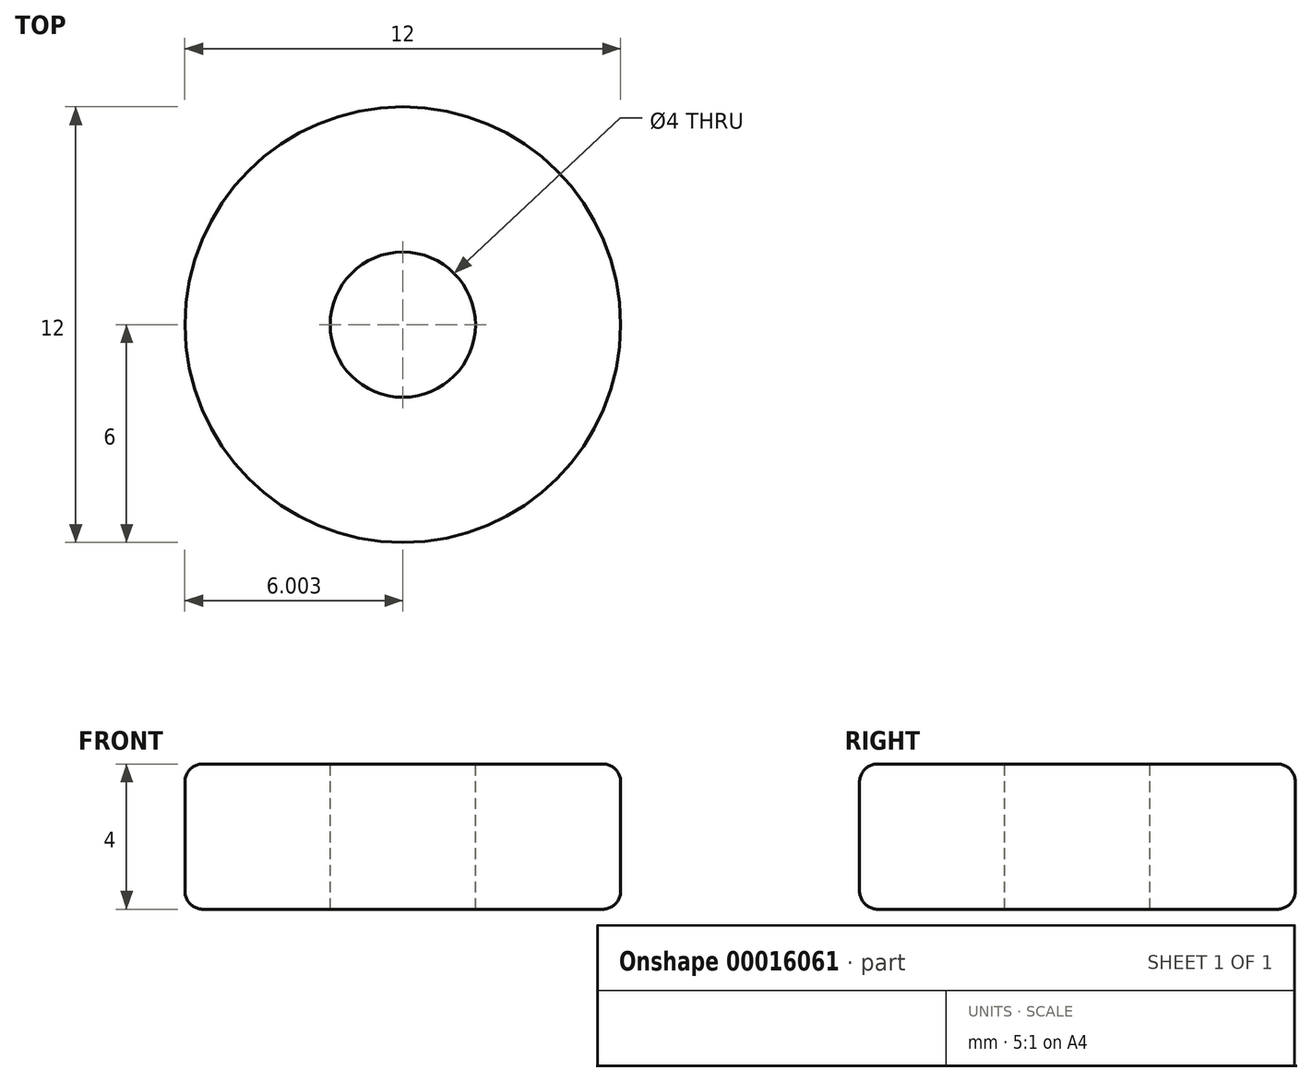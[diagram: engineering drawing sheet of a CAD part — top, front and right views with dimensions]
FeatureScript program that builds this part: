
annotation { "Feature Type Name" : "Feature", "Feature Type Description" : "" }
export const myFeature = defineFeature(function(context is Context, id is Id, definition is map)
    precondition{}
    {
        {
            var Q0;
            Q0=qCreatedBy(makeId("Top.planeOp"),FACE);
            var sketch = newSketch(context, id + "F0", { "sketchPlane" : qUnion([Q0])});
            skCircle(sketch, "E0", {"center": v(-26.95, 0) * mm, "radius": 6 * mm});
            skSolve(sketch);
        }
        {
            var Q0;
            Q0 = qSketchRegion(id + "F0", true);
            extrude(context, id + "F1", {"entities" : qUnion([Q0]), "depth" : 4 * mm});
        }
        {
            var Q0;
            Q0=makeQuery(id+"F1.opExtrude","CAP_FACE",FACE,{"disambiguationData":[OSD([sQuery(id+"F0.wireOp",EDGE,"E0")])],"isStart":false});
            var sketch = newSketch(context, id + "F2", { "sketchPlane" : qUnion([Q0])});
            skCircle(sketch, "E1", {"center": v(-26.95, 0) * mm, "radius": 2 * mm});
            skSolve(sketch);
        }
        {
            var Q0;
            Q0 = qSketchRegion(id + "F2", true);
            extrude(context, id + "F3", {"entities" : qUnion([Q0]), "operationType" : NewBodyOperationType.REMOVE, "endBound" : BoundingType.THROUGH_ALL, "oppositeDirection" : true, "depth" : 25 * mm});
        }
        {
            var Q0;
            Q0=makeQuery(id+"F1.opExtrude","CAP_EDGE",EDGE,{"disambiguationData":[OSD([sQuery(id+"F0.wireOp",EDGE,"E0")])],"isStart":true});
            var Q1;
            Q1=makeQuery(id+"F1.opExtrude","CAP_EDGE",EDGE,{"disambiguationData":[OSD([sQuery(id+"F0.wireOp",EDGE,"E0")])],"isStart":false});
            fillet(context, id + "F4", {"entities" : qUnion([Q0, Q1]), "radius" : .5 * mm, "tangentPropagation" : true, "allowEdgeOverflow" : false});
        }
    });
